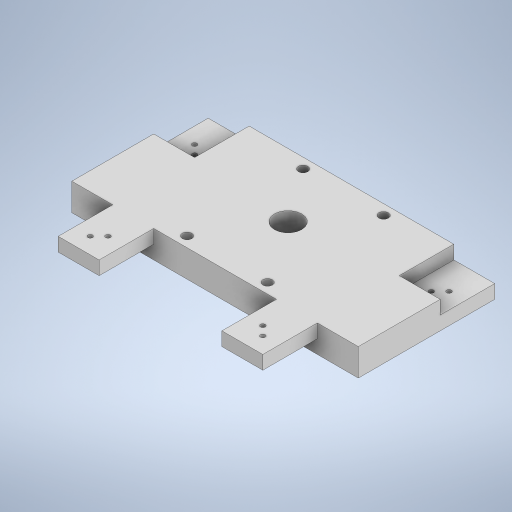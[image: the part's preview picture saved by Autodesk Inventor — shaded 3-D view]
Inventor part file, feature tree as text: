
AUTODESK INVENTOR PART (.ipt)
format: ipt  version: 2023 (Build 270158000, 158)  size: 341,504 bytes
history: native  units: mm
features: sketch x7, extrude x5, hole x2, other x1
ambient origin geometry x8: Origin, YZ Plane, XZ Plane, XY Plane, X Axis, Y Axis, Z Axis, Center Point
bodies: Body1 (feature_tree)
feature tree (15):
  other  "Sólido1"
  extrude  "Extrusión1"  Depth=100.0mm
  extrude  "Extrusión2"  Depth=20.0mm
  extrude  "Extrusión3"  Depth=59.0mm
  extrude  "Extrusión4"  Depth=39.0mm
  hole  "Agujero1"  [1 undecoded]
  extrude  "Extrusión6"  Depth=10.0mm TaperAngle=0.0deg
  hole  "Agujero3"  [1 undecoded]
  sketch  "Boceto1"  dims[d0=210.0mm d1=100.0mm]
  sketch  "Boceto2"  dims[d2=20.0mm d3=0.0mm d4=7.0mm d5=7.0mm d6=7.0mm d7=39.0mm]
  sketch  "Boceto3"  dims[d8=46.0mm d9=59.0mm]
  sketch  "Boceto4"  dims[d10=46.0mm d11=39.0mm]
  sketch  "Boceto5"  dims[d12=59.0mm d13=7.5mm]
  sketch  "Boceto6"  dims[d14=20.0mm d15=0.0mm d19=10.0mm d20=0.0mm]
  sketch  "Boceto8"  dims[d21=80.0mm d22=0.0mm d26=3.5mm d27=6.0mm d28=4.0mm d29=2.0mm d30=90.0deg d31=8.0mm d32=20.594885mm d33=10.0mm d34=10.0mm d35=40.0mm d36=0.0mm d37=6.5mm d38=6.5mm d41=3.5mm d42=3.5mm d43=11.749873mm d44=11.75mm d66=40.0mm d67=0.0mm d70=30.0mm d71=30.0mm d73=11.749873mm d74=40.0mm d75=29.999873mm d76=21.75mm d77=11.75mm d78=28.300341mm d79=11.749873mm d80=0.0mm d81=0.0mm d82=3.5mm d83=6.0mm d84=4.0mm d85=2.0mm d86=90.0deg d87=8.0mm d88=20.594885mm]
note: 2 required parameter values undecoded (feature->parameter linkage not recoverable at this tier; creation-order binding heuristic only, values carry confidence <= 0.55)
